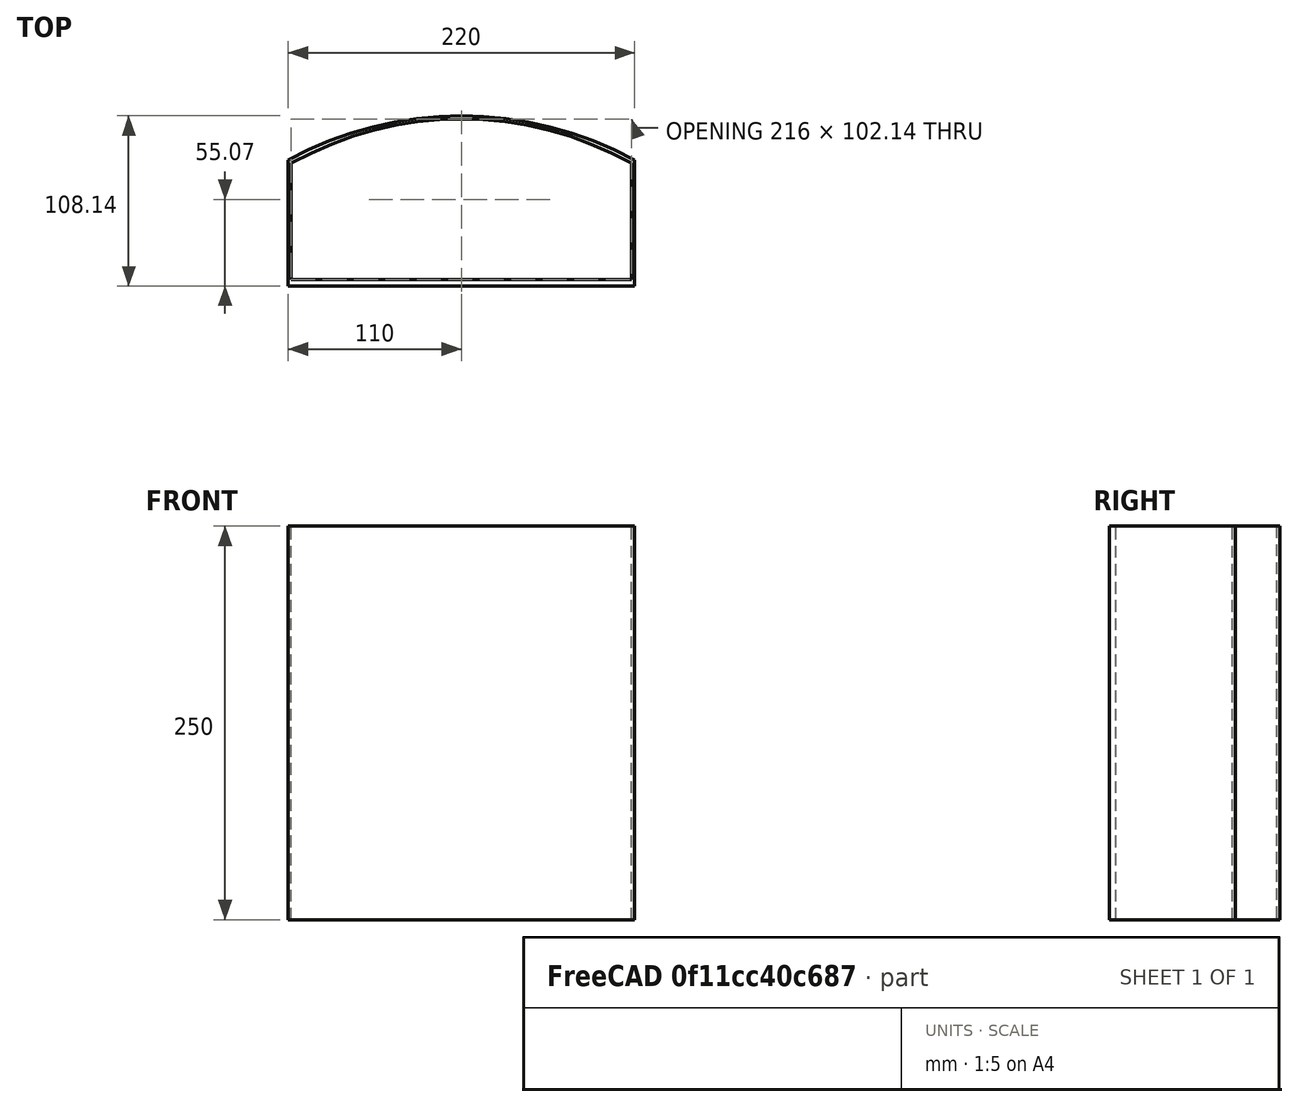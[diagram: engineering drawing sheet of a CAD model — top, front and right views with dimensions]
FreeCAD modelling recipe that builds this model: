
FCSTD DOCUMENT  (FreeCAD 0.22R38261 (Git))
Label: ящик на стену
License: All rights reserved
LicenseURL: https://en.wikipedia.org/wiki/All_rights_reserved
objects: Sketcher::SketchObject×1, PartDesign::Pad×1, PartDesign::Body×1, App::Part×1
note: 5 computed .brp shape members not serialized (recipe doc carries the construction recipe); baked Part::Feature solids carry a one-line shape summary decoded from their .brp

FEATURE [Sketcher::SketchObject] Sketch
  AttachmentSupport = -> [XY_Plane001]
  FullyConstrained = false
  MapMode = 5
  sketch-geometry (12):
    g0: LineSegment StartX=0 StartY=0 StartZ=0 EndX=220 EndY=0 EndZ=0
    g1: LineSegment StartX=0 StartY=0 StartZ=0 EndX=-1.42e-14 EndY=80 EndZ=0
    g2: LineSegment StartX=220 StartY=0 StartZ=0 EndX=220 EndY=80 EndZ=0
    g3: ArcOfCircle CenterX=110 CenterY=-120.926 CenterZ=0 NormalX=0 NormalY=0 NormalZ=1 AngleXU=0 Radius=229.066 StartAngle=1.0699 EndAngle=2.07169
    g4: LineSegment StartX=2 StartY=4 StartZ=0 EndX=218 EndY=4 EndZ=0
    g5: LineSegment StartX=2 StartY=4 StartZ=0 EndX=2 EndY=78 EndZ=0
    g6: LineSegment StartX=218 StartY=4 StartZ=0 EndX=218 EndY=78 EndZ=0
    g7: ArcOfCircle CenterX=110 CenterY=-115.179 CenterZ=0 NormalX=0 NormalY=0 NormalZ=1 AngleXU=0 Radius=221.319 StartAngle=1.06102 EndAngle=2.08058
    g8: LineSegment StartX=2 StartY=78 StartZ=0 EndX=110 EndY=106.14 EndZ=0
    g9: LineSegment StartX=110 StartY=106.14 StartZ=0 EndX=218 EndY=78 EndZ=0
    g10: LineSegment StartX=-1.42e-14 StartY=80 StartZ=0 EndX=110 EndY=108.14 EndZ=0
    g11: LineSegment StartX=110 StartY=108.14 StartZ=0 EndX=220 EndY=80 EndZ=0
  constraints (34):
    c: Coincident(g0,g-1)
    c: PointOnObject(g0,g-1)
    c: DistanceX(g0,g0) = 220
    c: Coincident(g1,g0)
    c: PointOnObject(g1,g-2)
    c: DistanceY(g1,g1) = 80
    c: Coincident(g2,g0)
    c: Vertical(g2)
    c: Equal(g1,g2)
    c: Coincident(g3,g1)
    c: Coincident(g3,g2)
    c: Horizontal(g4)
    c: DistanceY(g0,g4) = 4
    c: DistanceX(g4,g0) = 2
    c: DistanceX(g0,g4) = 2
    c: Coincident(g5,g4)
    c: Vertical(g5)
    c: DistanceY(g5,g1) = 2
    c: Coincident(g6,g4)
    c: Vertical(g6)
    c: Equal(g6,g5)
    c: Coincident(g7,g5)
    c: Coincident(g7,g6)
    c: Coincident(g8,g5)
    c: PointOnObject(g8,g7)
    c: Coincident(g9,g8)
    c: Coincident(g9,g6)
    c: Equal(g8,g9)
    c: Coincident(g10,g1)
    c: PointOnObject(g10,g3)
    c: Coincident(g11,g10)
    c: Coincident(g11,g2)
    c: Equal(g10,g11)
    c: DistanceY(g8,g10) = 2
FEATURE [PartDesign::Pad] Pad
  Direction = (0,0,1)
  Length = 250
  Length2 = 10
  Profile = -> Sketch
  ReferenceAxis = -> Sketch [N_Axis]
  Suppressed = false
  Type = 0
FEATURE [PartDesign::Body] Body
  AllowCompound = false
  Group = -> [Sketch,Pad]
  Origin = -> Origin001
  Tip = -> Pad
FEATURE [App::Part] Part
  Group = -> [Body]
  Origin = -> Origin
